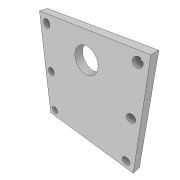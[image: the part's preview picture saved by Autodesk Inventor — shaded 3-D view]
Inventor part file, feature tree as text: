
AUTODESK INVENTOR PART (.ipt)
format: ipt  version: 2019 (Build 230136000, 136)  size: 114,688 bytes
history: native  units: in
note: dims shown in document units (in); Inventor stores cm internally (conversion verified against a paired STEP export)
features: extrude x2, sketch x2
ambient origin geometry x8: Origin, YZ Plane, XZ Plane, XY Plane, X Axis, Y Axis, Z Axis, Center Point
bodies: Solid1 (feature_tree)
feature tree (4):
  extrude  "Extrusion1"  Depth=5.1181in
  extrude  "Extrusion2"  Depth=0.3937in
  sketch  "Sketch1"  dims[d0=5.1181in d1=5.1181in]
  sketch  "Sketch2"  dims[d2=0.3937in d3=0.0in d4=0.3937in d5=4.3307in d6=0.3937in d7=0.3937in d8=0.3937in d9=0.3937in d10=0.3937in d11=0.3937in d12=2.5591in d13=0.3937in d14=0.3937in d15=2.5591in d16=1.1811in d17=1.1811in d18=0.0in d19=0.0in]
